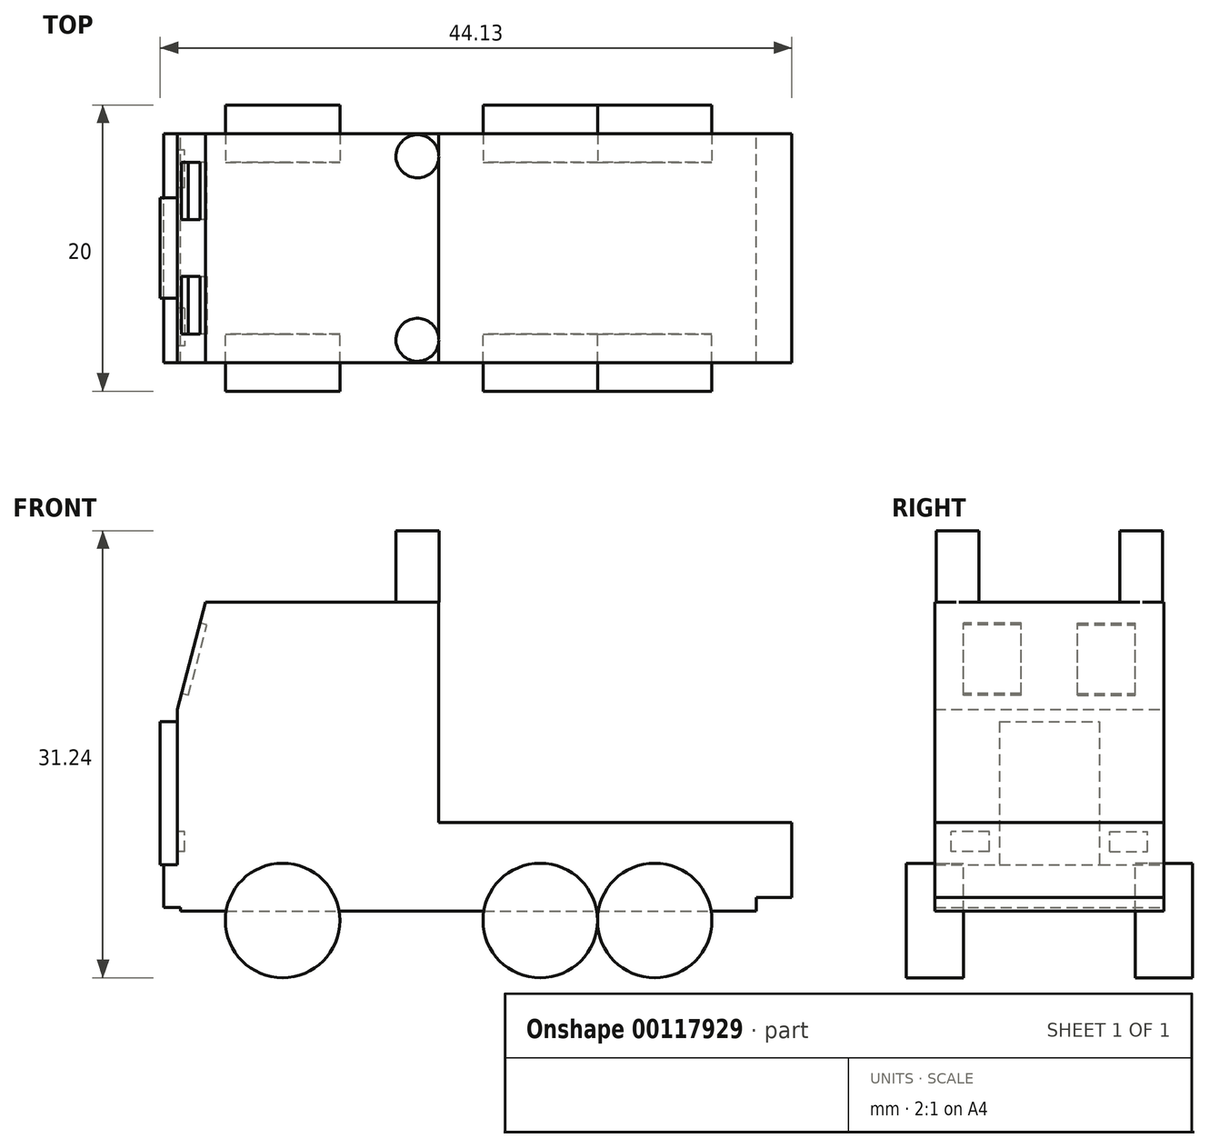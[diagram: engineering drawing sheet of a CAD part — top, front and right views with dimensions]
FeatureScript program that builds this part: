
annotation { "Feature Type Name" : "Feature", "Feature Type Description" : "" }
export const myFeature = defineFeature(function(context is Context, id is Id, definition is map)
    precondition{}
    {
        {
            var Q0;
            Q0=qCreatedBy(makeId("Front.planeOp"),FACE);
            cPlane(context, id + "F0", {"entities" : qUnion([Q0]), "cplaneType" : CPlaneType.OFFSET, "offset" : 6 * mm, "width" : 150 * mm, "height" : 150 * mm});
        }
        {
            var Q0;
            Q0=qCreatedBy(id+"F0.planeOp",FACE);
            var sketch = newSketch(context, id + "F1", { "sketchPlane" : qUnion([Q0])});
            skCircle(sketch, "E0", {"center": v(0, 4) * mm, "radius": 4 * mm});
            skCircle(sketch, "E1", {"center": v(18, 4) * mm, "radius": 4 * mm});
            skCircle(sketch, "E2", {"center": v(26, 4) * mm, "radius": 4 * mm});
            skSolve(sketch);
        }
        {
            var Q0;
            Q0 = qSketchRegion(id + "F1", true);
            extrude(context, id + "F2", {"entities" : qUnion([Q0]), "depth" : 4 * mm});
        }
        {
            var Q0;
            Q0=makeQuery(id+"F2.opExtrude","SWEPT_BODY",BODY,{"disambiguationData":[OSD([sQuery(id+"F1.wireOp",EDGE,"E0")])]});
            var Q1;
            Q1=makeQuery(id+"F2.opExtrude","SWEPT_BODY",BODY,{"disambiguationData":[OSD([sQuery(id+"F1.wireOp",EDGE,"E1")])]});
            var Q2;
            Q2=makeQuery(id+"F2.opExtrude","SWEPT_BODY",BODY,{"disambiguationData":[OSD([sQuery(id+"F1.wireOp",EDGE,"E2")])]});
            var Q3;
            Q3=qCreatedBy(makeId("Front.planeOp"),FACE);
            mirror(context, id + "F3", {"entities" : qUnion([Q0, Q1, Q2]), "mirrorPlane" : qUnion([Q3])});
        }
        {
            var Q0;
            Q0=qCreatedBy(makeId("Front.planeOp"),FACE);
            var sketch = newSketch(context, id + "F4", { "sketchPlane" : qUnion([Q0])});
            skLineSegment(sketch, "E3", {"start": v(-7.13, 4.64) * mm, "end": v(33.1, 4.64) * mm});
            skLineSegment(sketch, "E4", {"start": v(33.1, 4.64) * mm, "end": v(33.1, 5.62) * mm});
            skLineSegment(sketch, "E5", {"start": v(10.92, 10.86) * mm, "end": v(10.92, 26.24) * mm});
            skLineSegment(sketch, "E6", {"start": v(10.92, 26.24) * mm, "end": v(-5.4, 26.24) * mm});
            skLineSegment(sketch, "E7", {"start": v(-5.4, 26.24) * mm, "end": v(-7.35, 18.74) * mm});
            skLineSegment(sketch, "E8", {"start": v(-7.35, 18.74) * mm, "end": v(-7.35, 7.9) * mm});
            skLineSegment(sketch, "E9", {"start": v(-7.35, 7.9) * mm, "end": v(-8.3, 7.9) * mm});
            skLineSegment(sketch, "E10", {"start": v(-8.3, 7.9) * mm, "end": v(-8.3, 4.9) * mm});
            skLineSegment(sketch, "E11", {"start": v(-8.3, 4.9) * mm, "end": v(-7.13, 4.9) * mm});
            skLineSegment(sketch, "E12", {"start": v(-7.13, 4.9) * mm, "end": v(-7.13, 4.64) * mm});
            skLineSegment(sketch, "E13", {"start": v(33.1, 5.62) * mm, "end": v(35.58, 5.62) * mm});
            skLineSegment(sketch, "E14", {"start": v(35.58, 5.62) * mm, "end": v(35.58, 10.86) * mm});
            skLineSegment(sketch, "E15", {"start": v(35.58, 10.86) * mm, "end": v(10.92, 10.86) * mm});
            skSolve(sketch);
        }
        {
            var Q0;
            Q0 = qSketchRegion(id + "F4", true);
            extrude(context, id + "F5", {"entities" : qUnion([Q0]), "depth" : 8 * mm, "hasSecondDirection" : true, "secondDirectionOppositeDirection" : true, "secondDirectionDepth" : 8 * mm});
        }
        {
            var Q0;
            Q0=makeQuery(id+"F5.opExtrude","SWEPT_FACE",FACE,{"disambiguationData":[OSD([sQuery(id+"F4.wireOp",EDGE,"E9")])]});
            var sketch = newSketch(context, id + "F6", { "sketchPlane" : qUnion([Q0])});
            skLineSegment(sketch, "E16.bottom", {"start": v(-7.35, -3.5) * mm, "end": v(-8.55, -3.5) * mm});
            skLineSegment(sketch, "E16.top", {"start": v(-7.35, 3.5) * mm, "end": v(-8.55, 3.5) * mm});
            skLineSegment(sketch, "E16.left", {"start": v(-7.35, -3.5) * mm, "end": v(-7.35, 3.5) * mm});
            skLineSegment(sketch, "E16.right", {"start": v(-8.55, -3.5) * mm, "end": v(-8.55, 3.5) * mm});
            skPoint(sketch, "E16.middle", {"position": v(-7.95, 0) * mm});
            skSolve(sketch);
        }
        {
            var Q0;
            Q0 = qSketchRegion(id + "F6", true);
            extrude(context, id + "F7", {"entities" : qUnion([Q0]), "operationType" : NewBodyOperationType.ADD, "depth" : 10 * mm});
        }
        {
            var Q0;
            Q0=makeQuery(id+"F5.opExtrude","SWEPT_FACE",FACE,{"disambiguationData":[OSD([sQuery(id+"F4.wireOp",EDGE,"E7")])]});
            var sketch = newSketch(context, id + "F8", { "sketchPlane" : qUnion([Q0])});
            skLineSegment(sketch, "E17", {"start": v(0, 24.02) * mm, "end": v(0, 16.27) * mm, "construction": true});
            skLineSegment(sketch, "E18.bottom", {"start": v(-1.98, 17.43) * mm, "end": v(-6, 17.43) * mm});
            skLineSegment(sketch, "E18.top", {"start": v(-1.98, 22.5) * mm, "end": v(-6, 22.5) * mm});
            skLineSegment(sketch, "E18.left", {"start": v(-1.98, 17.43) * mm, "end": v(-1.98, 22.5) * mm});
            skLineSegment(sketch, "E18.right", {"start": v(-6, 17.43) * mm, "end": v(-6, 22.5) * mm});
            skPoint(sketch, "E18.middle", {"position": v(-4, 19.97) * mm});
            skLineSegment(sketch, "E19.MirrorCS", {"start": v(1.98, 17.43) * mm, "end": v(6, 17.43) * mm});
            skLineSegment(sketch, "E20.MirrorCS", {"start": v(6, 17.43) * mm, "end": v(6, 22.5) * mm});
            skLineSegment(sketch, "E21.MirrorCS", {"start": v(1.98, 22.5) * mm, "end": v(6, 22.5) * mm});
            skLineSegment(sketch, "E22.MirrorCS", {"start": v(1.98, 17.43) * mm, "end": v(1.98, 22.5) * mm});
            skSolve(sketch);
        }
        {
            var Q0;
            Q0 = qSketchRegion(id + "F8", true);
            extrude(context, id + "F9", {"entities" : qUnion([Q0]), "operationType" : NewBodyOperationType.REMOVE, "oppositeDirection" : true, "depth" : 0.5 * mm});
        }
        {
            var Q0;
            Q0=makeQuery(id+"F5.opExtrude","SWEPT_FACE",FACE,{"disambiguationData":[OSD([sQuery(id+"F4.wireOp",EDGE,"E8")])]});
            var sketch = newSketch(context, id + "F10", { "sketchPlane" : qUnion([Q0])});
            skLineSegment(sketch, "E23.bottom", {"start": v(-4.2, 8.81) * mm, "end": v(-6.85, 8.81) * mm});
            skLineSegment(sketch, "E23.top", {"start": v(-4.2, 10.2) * mm, "end": v(-6.85, 10.2) * mm});
            skLineSegment(sketch, "E23.left", {"start": v(-4.2, 8.81) * mm, "end": v(-4.2, 10.2) * mm});
            skLineSegment(sketch, "E23.right", {"start": v(-6.85, 8.81) * mm, "end": v(-6.85, 10.2) * mm});
            skPoint(sketch, "E23.middle", {"position": v(-5.53, 9.5) * mm});
            skLineSegment(sketch, "E24", {"start": v(0, 0) * mm, "end": v(0, 29.81) * mm});
            skLineSegment(sketch, "E25.MirrorCS", {"start": v(4.2, 8.81) * mm, "end": v(4.2, 10.2) * mm});
            skLineSegment(sketch, "E26.MirrorCS", {"start": v(4.2, 8.81) * mm, "end": v(6.85, 8.81) * mm});
            skLineSegment(sketch, "E27.MirrorCS", {"start": v(4.2, 10.2) * mm, "end": v(6.85, 10.2) * mm});
            skLineSegment(sketch, "E28.MirrorCS", {"start": v(6.85, 8.81) * mm, "end": v(6.85, 10.2) * mm});
            skSolve(sketch);
        }
        {
            var Q0;
            Q0 = qSketchRegion(id + "F10", true);
            extrude(context, id + "F11", {"entities" : qUnion([Q0]), "operationType" : NewBodyOperationType.REMOVE, "oppositeDirection" : true, "depth" : 0.5 * mm});
        }
        {
            var Q0;
            Q0=makeQuery(id+"F5.opExtrude","SWEPT_FACE",FACE,{"disambiguationData":[OSD([sQuery(id+"F4.wireOp",EDGE,"E6")])]});
            var sketch = newSketch(context, id + "F12", { "sketchPlane" : qUnion([Q0])});
            skCircle(sketch, "E29", {"center": v(9.42, 6.41) * mm, "radius": 1.5 * mm});
            skCircle(sketch, "E30.MirrorC", {"center": v(9.42, -6.41) * mm, "radius": 1.5 * mm});
            skSolve(sketch);
        }
        {
            var Q0;
            Q0 = qSketchRegion(id + "F12", true);
            extrude(context, id + "F13", {"entities" : qUnion([Q0]), "operationType" : NewBodyOperationType.ADD, "depth" : 5 * mm});
        }
    });
